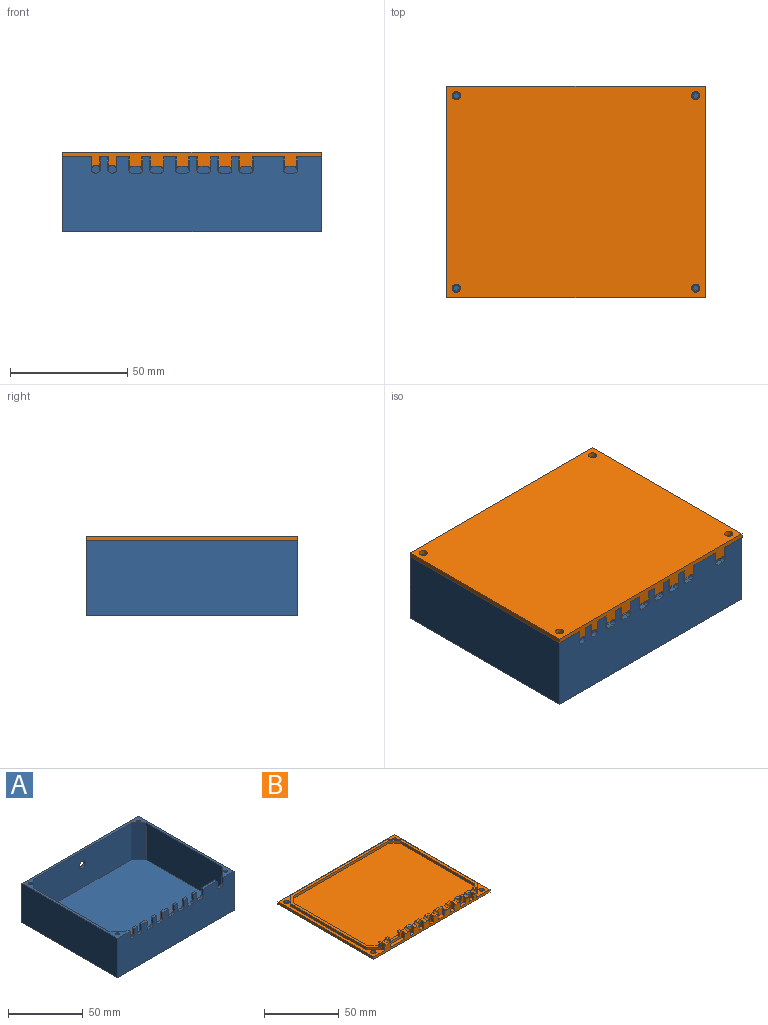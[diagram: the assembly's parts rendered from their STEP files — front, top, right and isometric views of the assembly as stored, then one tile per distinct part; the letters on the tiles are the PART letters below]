
ASSEMBLY  parts=2 mates=1
PART A: 73 faces, bbox 110x90x32 mm
  f0: plane 92x30mm, normal (0,1,0), area 2420.2mm2, adj f1,f2,f3,f4,f5,f6,f7,f8
  f1: plane 3x2mm, normal (0,0,1), area 6mm2, adj f0,f12,f66,f71
  f2: plane 5x2mm, normal (0,0,1), area 10mm2, adj f0,f12,f61,f68
  f3: plane 3x2mm, normal (0,0,1), area 6mm2, adj f0,f12,f56,f65
  f4: plane 5x2mm, normal (0,0,1), area 10mm2, adj f0,f12,f51,f60
  f5: plane 3x2mm, normal (0,0,1), area 6mm2, adj f0,f12,f46,f55
  f6: plane 3x2mm, normal (0,0,1), area 6mm2, adj f0,f12,f41,f50
  f7: plane 3x2mm, normal (0,0,1), area 6mm2, adj f0,f12,f36,f45
  f8: plane 13x2mm, normal (0,0,1), area 26mm2, adj f0,f12,f31,f40
  f9: plane 110x90mm, normal (0,0,1), area 686.4mm2, adj f0,f10,f11,f12,f13,f15,f16,f17
  f10: plane 110x32mm, normal (0,1,0), area 3491.7mm2, adj f9,f11,f13,f14,f72
  f11: plane 90x32mm, normal (-1,0,0), area 2880mm2, adj f9,f10,f12,f14
  f12: plane 110x32mm, normal (0,-1,0), area 3180.2mm2, adj f1,f2,f3,f4,f5,f6,f7,f8
  f13: plane 90x32mm, normal (1,0,0), area 2880mm2, adj f9,f10,f12,f14
  f14: plane 110x90mm, normal (0,0,-1), area 9900mm2, adj f10,f11,f12,f13
  f15: plane 30x7mm, normal (0.71,0.71,0), area 297mm2, adj f0,f9,f16,f27
  f16: plane 72x30mm, normal (1,0,0), area 2160mm2, adj f9,f15,f17,f27
  f17: plane 30x7mm, normal (0.71,-0.71,0), area 297mm2, adj f9,f16,f18,f27
  f18: plane 92x30mm, normal (0,-1,0), area 2731.7mm2, adj f9,f17,f19,f27,f72
  f19: plane 30x7mm, normal (-0.71,-0.71,0), area 297mm2, adj f9,f18,f20,f27
  f20: plane 72x30mm, normal (-1,0,0), area 2160mm2, adj f9,f19,f24,f27
  f21: cylinder r=1.25mm len=30mm, axis (0,0,-1), area 235.6mm2, adj f9,f30
  f22: cylinder r=1.25mm len=30mm, axis (0,0,-1), area 235.6mm2, adj f9,f29
  f23: cylinder r=1.25mm len=30mm, axis (0,0,-1), area 235.6mm2, adj f9,f28
  f24: plane 30x7mm, normal (-0.71,0.71,0), area 297mm2, adj f0,f9,f20,f27
  f25: cylinder r=1.25mm len=30mm, axis (0,0,-1), area 235.6mm2, adj f9,f26
  f26: plane 2.5x2.5mm, normal (0,0,1), area 4.9mm2, adj f25
  f27: plane 106x86mm, normal (0,0,1), area 9018mm2, adj f0,f15,f16,f17,f18,f19,f20,f24
  f28: plane 2.5x2.5mm, normal (0,0,1), area 4.9mm2, adj f23
  f29: plane 2.5x2.5mm, normal (0,0,1), area 4.9mm2, adj f22
  f30: plane 2.5x2.5mm, normal (0,0,1), area 4.9mm2, adj f21
  f31: plane 5.5x2mm, normal (1,0,0), area 11mm2, adj f0,f8,f12,f32
  f32: cylinder r=1.5mm len=2mm, axis (0,-1,0), area 4.7mm2, adj f0,f12,f31,f33
  f33: plane 3x2mm, normal (0,0,1), area 6mm2, adj f0,f12,f32,f34
  f34: cylinder r=1.5mm len=2mm, axis (0,-1,0), area 4.7mm2, adj f0,f12,f33,f35
  f35: plane 5.5x2mm, normal (-1,0,0), area 11mm2, adj f0,f9,f12,f34
  f36: plane 5.5x2mm, normal (1,0,0), area 11mm2, adj f0,f7,f12,f37
  f37: cylinder r=1.5mm len=2mm, axis (0,-1,0), area 4.7mm2, adj f0,f12,f36,f38
  f38: plane 3x2mm, normal (0,0,1), area 6mm2, adj f0,f12,f37,f39
  f39: cylinder r=1.5mm len=2mm, axis (0,-1,0), area 4.7mm2, adj f0,f12,f38,f40
  f40: plane 5.5x2mm, normal (-1,0,0), area 11mm2, adj f0,f8,f12,f39
  f41: plane 5.5x2mm, normal (1,0,0), area 11mm2, adj f0,f6,f12,f42
  f42: cylinder r=1.5mm len=2mm, axis (0,-1,0), area 4.7mm2, adj f0,f12,f41,f43
  f43: plane 3x2mm, normal (0,0,1), area 6mm2, adj f0,f12,f42,f44
  f44: cylinder r=1.5mm len=2mm, axis (0,-1,0), area 4.7mm2, adj f0,f12,f43,f45
  f45: plane 5.5x2mm, normal (-1,0,0), area 11mm2, adj f0,f7,f12,f44
  f46: plane 5.5x2mm, normal (1,0,0), area 11mm2, adj f0,f5,f12,f47
  f47: cylinder r=1.5mm len=2mm, axis (0,-1,0), area 4.7mm2, adj f0,f12,f46,f48
  f48: plane 3x2mm, normal (0,0,1), area 6mm2, adj f0,f12,f47,f49
  f49: cylinder r=1.5mm len=2mm, axis (0,-1,0), area 4.7mm2, adj f0,f12,f48,f50
  f50: plane 5.5x2mm, normal (-1,0,0), area 11mm2, adj f0,f6,f12,f49
  f51: plane 5.5x2mm, normal (1,0,0), area 11mm2, adj f0,f4,f12,f52
  f52: cylinder r=1.5mm len=2mm, axis (0,-1,0), area 4.7mm2, adj f0,f12,f51,f53
  f53: plane 3x2mm, normal (0,0,1), area 6mm2, adj f0,f12,f52,f54
  f54: cylinder r=1.5mm len=2mm, axis (0,-1,0), area 4.7mm2, adj f0,f12,f53,f55
  f55: plane 5.5x2mm, normal (-1,0,0), area 11mm2, adj f0,f5,f12,f54
  f56: plane 5.5x2mm, normal (1,0,0), area 11mm2, adj f0,f3,f12,f57
  f57: cylinder r=1.5mm len=2mm, axis (0,-1,0), area 4.7mm2, adj f0,f12,f56,f58
  f58: plane 3x2mm, normal (0,0,1), area 6mm2, adj f0,f12,f57,f59
  f59: cylinder r=1.5mm len=2mm, axis (0,-1,0), area 4.7mm2, adj f0,f12,f58,f60
  f60: plane 5.5x2mm, normal (-1,0,0), area 11mm2, adj f0,f4,f12,f59
  f61: plane 5.5x2mm, normal (1,0,0), area 11mm2, adj f0,f2,f12,f62
  f62: cylinder r=1.5mm len=2mm, axis (0,-1,0), area 4.7mm2, adj f0,f12,f61,f63
  f63: plane 3x2mm, normal (0,0,1), area 6mm2, adj f0,f12,f62,f64
  f64: cylinder r=1.5mm len=2mm, axis (0,-1,0), area 4.7mm2, adj f0,f12,f63,f65
  f65: plane 5.5x2mm, normal (-1,0,0), area 11mm2, adj f0,f3,f12,f64
  f66: plane 5x2mm, normal (1,0,0), area 10mm2, adj f0,f1,f12,f67
  f67: cylinder r=2mm len=4mm, axis (0,-1,0), area 12.6mm2, adj f0,f12,f66,f68
  f68: plane 5x2mm, normal (-1,0,0), area 10mm2, adj f0,f2,f12,f67
  f69: plane 5x2mm, normal (1,0,0), area 10mm2, adj f0,f9,f12,f70
  f70: cylinder r=2mm len=4mm, axis (0,-1,0), area 12.6mm2, adj f0,f12,f69,f71
  f71: plane 5x2mm, normal (-1,0,0), area 10mm2, adj f0,f1,f12,f70
  f72: cylinder r=3mm len=6mm, axis (0,1,0), area 37.7mm2, adj f10,f18
PART B: 106 faces, bbox 110x90x7.5 mm
  f0: plane 5.31x3.6mm, normal (0,-1,0), area 19.1mm2, adj f1,f86,f103,f104
  f1: plane 3.6x2.4mm, normal (0,0,1), area 8.6mm2, adj f0,f21,f103,f104
  f2: plane 5.6x2.4mm, normal (0,0,1), area 13.4mm2, adj f21,f36,f99,f102
  f3: plane 5.31x3.13mm, normal (0,-1,0), area 13mm2, adj f10,f17,f35,f83,f84,f105
  f4: plane 13.6x2.4mm, normal (0,0,1), area 32.6mm2, adj f5,f21,f94,f100
  f5: plane 13.6x5.5mm, normal (0,-1,0), area 41.1mm2, adj f4,f30,f47,f53,f54,f55,f94,f100
  f6: plane 3.6x2.4mm, normal (0,0,1), area 8.6mm2, adj f7,f21,f97,f98
  f7: plane 5.5x3.6mm, normal (0,-1,0), area 19.8mm2, adj f6,f61,f97,f98
  f8: plane 5.6x2.4mm, normal (0,0,1), area 13.4mm2, adj f9,f21,f89,f96
  f9: plane 5.6x5.5mm, normal (0,-1,0), area 30.8mm2, adj f8,f65,f89,f96
  f10: plane 110x90mm, normal (0,0,1), area 780.3mm2, adj f3,f11,f19,f20,f21,f22,f23,f24
  f11: plane 5.5x1.13mm, normal (0,-1,0), area 6mm2, adj f10,f17,f37,f51,f52,f95
  f12: plane 3.6x2.4mm, normal (0,0,1), area 8.6mm2, adj f13,f21,f92,f101
  f13: plane 5.5x3.6mm, normal (0,-1,0), area 19.8mm2, adj f12,f77,f92,f101
  f14: plane 3.6x2.4mm, normal (0,0,1), area 8.6mm2, adj f15,f21,f90,f93
  f15: plane 5.5x3.6mm, normal (0,-1,0), area 19.8mm2, adj f14,f73,f90,f93
  f16: plane 5.5x3.6mm, normal (0,-1,0), area 19.8mm2, adj f27,f69,f88,f91
  f17: plane 105.2x85.2mm, normal (0,0,1), area 535.6mm2, adj f3,f11,f31,f32,f33,f34,f35,f37
  f18: plane 2x1.49mm, normal (0,0,1), area 3mm2, adj f36,f44,f56,f82
  f19: plane 110x2mm, normal (0,1,0), area 220mm2, adj f10,f20,f26,f28
  f20: plane 90x2mm, normal (-1,0,0), area 180mm2, adj f10,f19,f21,f28
  f21: plane 110x7.5mm, normal (0,-1,0), area 405mm2, adj f1,f2,f4,f6,f8,f10,f12,f14
  f22: cylinder r=1.75mm len=3.5mm, axis (0,0,-1), area 22mm2, adj f10,f28
  f23: cylinder r=1.75mm len=3.5mm, axis (0,0,-1), area 22mm2, adj f10,f28
  f24: cylinder r=1.75mm len=3.5mm, axis (0,0,-1), area 22mm2, adj f10,f28
  f25: cylinder r=1.75mm len=3.5mm, axis (0,0,-1), area 22mm2, adj f10,f28
  f26: plane 90x2mm, normal (1,0,0), area 180mm2, adj f10,f19,f21,f28
  f27: plane 3.6x2.4mm, normal (0,0,1), area 8.6mm2, adj f16,f21,f88,f91
  f28: plane 110x90mm, normal (0,0,-1), area 9861.5mm2, adj f19,f20,f21,f22,f23,f24,f25,f26
  f29: plane 101.2x81.2mm, normal (0,0,1), area 8154.9mm2, adj f39,f40,f41,f42,f43,f44,f45,f46
  f30: plane 9.63x2mm, normal (0,0,1), area 19.3mm2, adj f5,f44,f53,f55
  f31: plane 6.77x6.77mm, normal (-0.71,0.71,0), area 19.1mm2, adj f10,f17,f32,f38
  f32: plane 91.67x2mm, normal (0,1,0), area 183.3mm2, adj f10,f17,f31,f33
  f33: plane 6.77x6.77mm, normal (0.71,0.71,0), area 19.1mm2, adj f10,f17,f32,f34
  f34: plane 71.67x2mm, normal (1,0,0), area 143.3mm2, adj f10,f17,f33,f35
  f35: plane 6.77x6.77mm, normal (0.71,-0.71,0), area 19.1mm2, adj f3,f10,f17,f34
  f36: plane 5.6x5.5mm, normal (0,-1,0), area 25.2mm2, adj f2,f18,f56,f57,f81,f82,f99,f102
  f37: plane 6.77x6.77mm, normal (-0.71,-0.71,0), area 19.1mm2, adj f10,f11,f17,f38
  f38: plane 71.67x2mm, normal (-1,0,0), area 143.3mm2, adj f10,f17,f31,f37
  f39: plane 5.59x5.59mm, normal (0.71,-0.71,0), area 15.8mm2, adj f17,f29,f40,f46
  f40: plane 90.01x2mm, normal (0,-1,0), area 180mm2, adj f17,f29,f39,f41
  f41: plane 5.59x5.59mm, normal (-0.71,-0.71,0), area 15.8mm2, adj f17,f29,f40,f42
  f42: plane 70.01x2mm, normal (-1,0,0), area 140mm2, adj f17,f29,f41,f43
  f43: plane 5.59x5.59mm, normal (-0.71,0.71,0), area 15.8mm2, adj f17,f29,f42,f44
  f44: plane 90.78x5.5mm, normal (0,1,0), area 396.1mm2, adj f17,f18,f29,f30,f43,f45,f47,f48
  f45: plane 5.59x5.59mm, normal (0.71,0.71,0), area 15.8mm2, adj f17,f29,f44,f46
  f46: plane 70.01x2mm, normal (1,0,0), area 140mm2, adj f17,f29,f39,f45
  f47: plane 2x1.95mm, normal (0,0,1), area 3.9mm2, adj f5,f44,f48,f53
  f48: cylinder r=1.5mm len=4.4mm, axis (0,-1,0), area 10.4mm2, adj f21,f44,f47,f49,f94
  f49: plane 4.4x2.4mm, normal (0,0,1), area 10.6mm2, adj f21,f44,f48,f50
  f50: cylinder r=1.5mm len=4.4mm, axis (0,-1,0), area 10.4mm2, adj f21,f44,f49,f51,f95
  f51: plane 2x1.08mm, normal (0,0,1), area 2.2mm2, adj f11,f44,f50,f52
  f52: plane 3.5x2mm, normal (-1,0,0), area 7mm2, adj f11,f17,f44,f51
  f53: plane 3.5x2mm, normal (1,0,0), area 7mm2, adj f5,f30,f44,f47
  f54: plane 2.01x2mm, normal (0,0,1), area 4mm2, adj f5,f44,f55,f80
  f55: plane 3.5x2mm, normal (-1,0,0), area 7mm2, adj f5,f30,f44,f54
  f56: plane 3.5x2mm, normal (1,0,0), area 7mm2, adj f18,f36,f44,f57
  f57: plane 2x2mm, normal (0,0,1), area 4mm2, adj f36,f44,f56,f58
  f58: cylinder r=1.5mm len=4.4mm, axis (0,-1,0), area 10.4mm2, adj f21,f44,f57,f59,f99
  f59: plane 4.4x2.4mm, normal (0,0,1), area 10.6mm2, adj f21,f44,f58,f60
  f60: cylinder r=1.5mm len=4.4mm, axis (0,-1,0), area 10.4mm2, adj f21,f44,f59,f61,f98
  f61: plane 3.6x2mm, normal (0,0,1), area 7.2mm2, adj f7,f44,f60,f62
  f62: cylinder r=1.5mm len=4.4mm, axis (0,-1,0), area 10.4mm2, adj f21,f44,f61,f63,f97
  f63: plane 4.4x2.4mm, normal (0,0,1), area 10.6mm2, adj f21,f44,f62,f64
  f64: cylinder r=1.5mm len=4.4mm, axis (0,-1,0), area 10.4mm2, adj f21,f44,f63,f65,f96
  f65: plane 5.6x2mm, normal (0,0,1), area 11.2mm2, adj f9,f44,f64,f66
  f66: cylinder r=1.5mm len=4.4mm, axis (0,-1,0), area 10.4mm2, adj f21,f44,f65,f67,f89
  f67: plane 4.4x2.4mm, normal (0,0,1), area 10.6mm2, adj f21,f44,f66,f68
  f68: cylinder r=1.5mm len=4.4mm, axis (0,-1,0), area 10.4mm2, adj f21,f44,f67,f69,f88
  f69: plane 3.6x2mm, normal (0,0,1), area 7.2mm2, adj f16,f44,f68,f70
  f70: cylinder r=1.5mm len=4.4mm, axis (0,-1,0), area 10.4mm2, adj f21,f44,f69,f71,f91
  f71: plane 4.4x2.4mm, normal (0,0,1), area 10.6mm2, adj f21,f44,f70,f72
  f72: cylinder r=1.5mm len=4.4mm, axis (0,-1,0), area 10.4mm2, adj f21,f44,f71,f73,f90
  f73: plane 3.6x2mm, normal (0,0,1), area 7.2mm2, adj f15,f44,f72,f74
  f74: cylinder r=1.5mm len=4.4mm, axis (0,-1,0), area 10.4mm2, adj f21,f44,f73,f75,f93
  f75: plane 4.4x2.4mm, normal (0,0,1), area 10.6mm2, adj f21,f44,f74,f76
  f76: cylinder r=1.5mm len=4.4mm, axis (0,-1,0), area 10.4mm2, adj f21,f44,f75,f77,f92
  f77: plane 3.6x2mm, normal (0,0,1), area 7.2mm2, adj f13,f44,f76,f78
  f78: cylinder r=1.5mm len=4.4mm, axis (0,-1,0), area 10.4mm2, adj f21,f44,f77,f79,f101
  f79: plane 4.4x2.4mm, normal (0,0,1), area 10.6mm2, adj f21,f44,f78,f80
  f80: cylinder r=1.5mm len=4.4mm, axis (0,-1,0), area 10.4mm2, adj f21,f44,f54,f79,f100
  f81: plane 2.1x2mm, normal (0,0,1), area 4.2mm2, adj f36,f44,f82,f87
  f82: plane 3.3x2mm, normal (-1,0,0), area 6.6mm2, adj f18,f36,f44,f81
  f83: plane 3.31x2mm, normal (1,0,0), area 6.6mm2, adj f3,f17,f44,f84
  f84: plane 2.03x2mm, normal (0,0,1), area 4.1mm2, adj f3,f44,f83,f85
  f85: cylinder r=1.7mm len=4.4mm, axis (0,-1,0), area 23.5mm2, adj f21,f44,f84,f86,f104,f105
  f86: plane 3.6x2mm, normal (0,0,1), area 7.2mm2, adj f0,f44,f85,f87
  f87: cylinder r=1.7mm len=4.4mm, axis (0,-1,0), area 23.5mm2, adj f21,f44,f81,f86,f102,f103
  f88: plane 5.5x2.4mm, normal (-1,0,0), area 13.2mm2, adj f16,f21,f27,f68
  f89: plane 5.5x2.4mm, normal (1,0,0), area 13.2mm2, adj f8,f9,f21,f66
  f90: plane 5.5x2.4mm, normal (-1,0,0), area 13.2mm2, adj f14,f15,f21,f72
  f91: plane 5.5x2.4mm, normal (1,0,0), area 13.2mm2, adj f16,f21,f27,f70
  f92: plane 5.5x2.4mm, normal (-1,0,0), area 13.2mm2, adj f12,f13,f21,f76
  f93: plane 5.5x2.4mm, normal (1,0,0), area 13.2mm2, adj f14,f15,f21,f74
  f94: plane 5.5x2.4mm, normal (1,0,0), area 13.2mm2, adj f4,f5,f21,f48
  f95: plane 5.5x2.4mm, normal (-1,0,0), area 13.2mm2, adj f10,f11,f21,f50
  f96: plane 5.5x2.4mm, normal (-1,0,0), area 13.2mm2, adj f8,f9,f21,f64
  f97: plane 5.5x2.4mm, normal (1,0,0), area 13.2mm2, adj f6,f7,f21,f62
  f98: plane 5.5x2.4mm, normal (-1,0,0), area 13.2mm2, adj f6,f7,f21,f60
  f99: plane 5.5x2.4mm, normal (1,0,0), area 13.2mm2, adj f2,f21,f36,f58
  f100: plane 5.5x2.4mm, normal (-1,0,0), area 13.2mm2, adj f4,f5,f21,f80
  f101: plane 5.5x2.4mm, normal (1,0,0), area 13.2mm2, adj f12,f13,f21,f78
  f102: plane 5.3x2.4mm, normal (-1,0,0), area 12.7mm2, adj f2,f21,f36,f87
  f103: plane 5.3x2.4mm, normal (1,0,0), area 12.7mm2, adj f0,f1,f21,f87
  f104: plane 5.31x2.4mm, normal (-1,0,0), area 12.8mm2, adj f0,f1,f21,f85
  f105: plane 5.31x2.4mm, normal (1,0,0), area 12.8mm2, adj f3,f10,f21,f85
PLACE A t=(-12.05,0.11,6.85)mm fixed
PLACE B rot(axis=(0,1,0),180deg) t=(-12.05,0.11,40.85)mm
MATE fastened B.f25 <-> A.f25  axis (0,0,-1) through (-63.05,-40.89,38.85)mm
